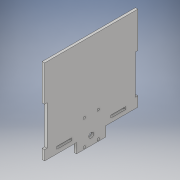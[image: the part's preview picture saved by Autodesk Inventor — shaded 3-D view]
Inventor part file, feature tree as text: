
AUTODESK INVENTOR PART (.ipt)
format: ipt  version: 2019 (Build 230136000, 136)  size: 226,304 bytes
history: native  units: in
note: dims shown in document units (in); Inventor stores cm internally (conversion verified against a paired STEP export)
features: extrude x10, sketch x10
ambient origin geometry x8: Origin, YZ Plane, XZ Plane, XY Plane, X Axis, Y Axis, Z Axis, Center Point
bodies: Solid1 (feature_tree)
feature tree (20):
  extrude  "Extrusion1"  Depth=4.5in
  extrude  "Extrusion2"  Depth=0.125in
  extrude  "Extrusion3"  Depth=0.118in
  extrude  "Extrusion5"  Depth=0.118in
  extrude  "Extrusion6"  Depth=0.1in
  extrude  "Extrusion7"  Depth=0.25in
  extrude  "Extrusion8"  Depth=0.354in
  extrude  "Extrusion9"  Depth=0.125in
  extrude  "Extrusion10"  Depth=1.299in
  extrude  "Extrusion11"  Depth=0.75in
  sketch  "Sketch1"  dims[d0=4.5in d1=3.836in]
  sketch  "Sketch2"  dims[d2=0.125in d3=0.0in d4=0.709in]
  sketch  "Sketch3"  dims[d5=0.118in d6=0.118in]
  sketch  "Sketch4"  dims[d7=0.118in d8=0.118in]
  sketch  "Sketch5"  dims[d11=0.709in d12=0.1in]
  sketch  "Sketch6"  dims[d13=0.125in d14=0.0in d15=0.25in]
  sketch  "Sketch7"  dims[d16=2.25in d17=0.354in]
  sketch  "Sketch8"  dims[d18=0.125in d19=0.0in d28=0.1in]
  sketch  "Sketch9"  dims[d29=1.299in d30=1.299in]
  sketch  "Sketch10"  dims[d31=0.125in d33=0.75in d34=0.5in d35=0.125in d36=0.0in d37=1.5in d38=0.5in d39=1.5in d40=0.125in d41=0.0in d42=0.5in d43=0.711in d44=1.5in d45=0.75in d46=0.125in d47=0.125in d48=0.0in d49=0.125in d50=0.125in d51=0.0in d52=0.125in d53=0.0in d54=0.125in d55=0.125in d56=2.0in d57=2.0in d58=0.5in d59=0.125in d60=0.0in d61=0.125in d62=0.0in d65=1.8955in d66=0.0in d67=1.0in d68=0.125in d69=0.0in]
